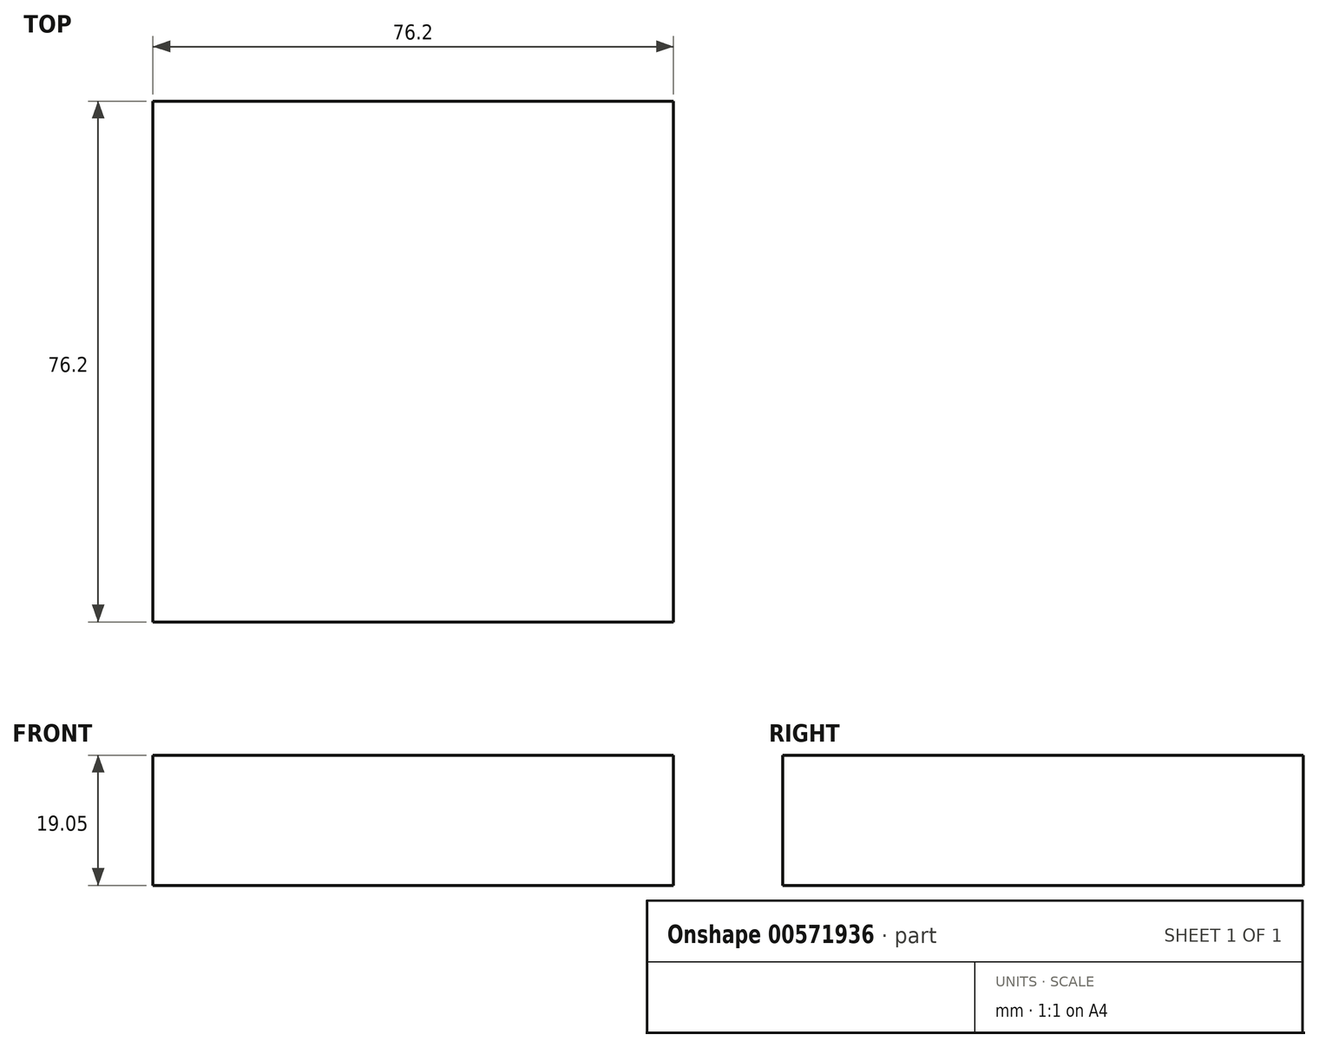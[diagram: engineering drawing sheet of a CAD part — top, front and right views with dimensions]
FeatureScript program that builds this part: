
annotation { "Feature Type Name" : "Feature", "Feature Type Description" : "" }
export const myFeature = defineFeature(function(context is Context, id is Id, definition is map)
    precondition{}
    {
        {
            var Q0;
            Q0=qCreatedBy(makeId("Top.planeOp"),FACE);
            var sketch = newSketch(context, id + "F0", { "sketchPlane" : qUnion([Q0])});
            skLineSegment(sketch, "E0", {"start": v(-117.32, -47.8) * mm, "end": v(-41.12, -47.8) * mm});
            skLineSegment(sketch, "E1", {"start": v(-41.12, -47.8) * mm, "end": v(-41.12, 28.4) * mm});
            skLineSegment(sketch, "E2", {"start": v(-41.12, 28.4) * mm, "end": v(-117.32, 28.4) * mm});
            skLineSegment(sketch, "E3", {"start": v(-117.32, 28.4) * mm, "end": v(-117.32, -47.8) * mm});
            skSolve(sketch);
        }
        {
            var Q0;
            Q0 = qSketchRegion(id + "F0", true);
            extrude(context, id + "F1", {"entities" : qUnion([Q0]), "depth" : 19.05 * mm, "offsetDistance" : 25.4 * mm});
        }
    });
